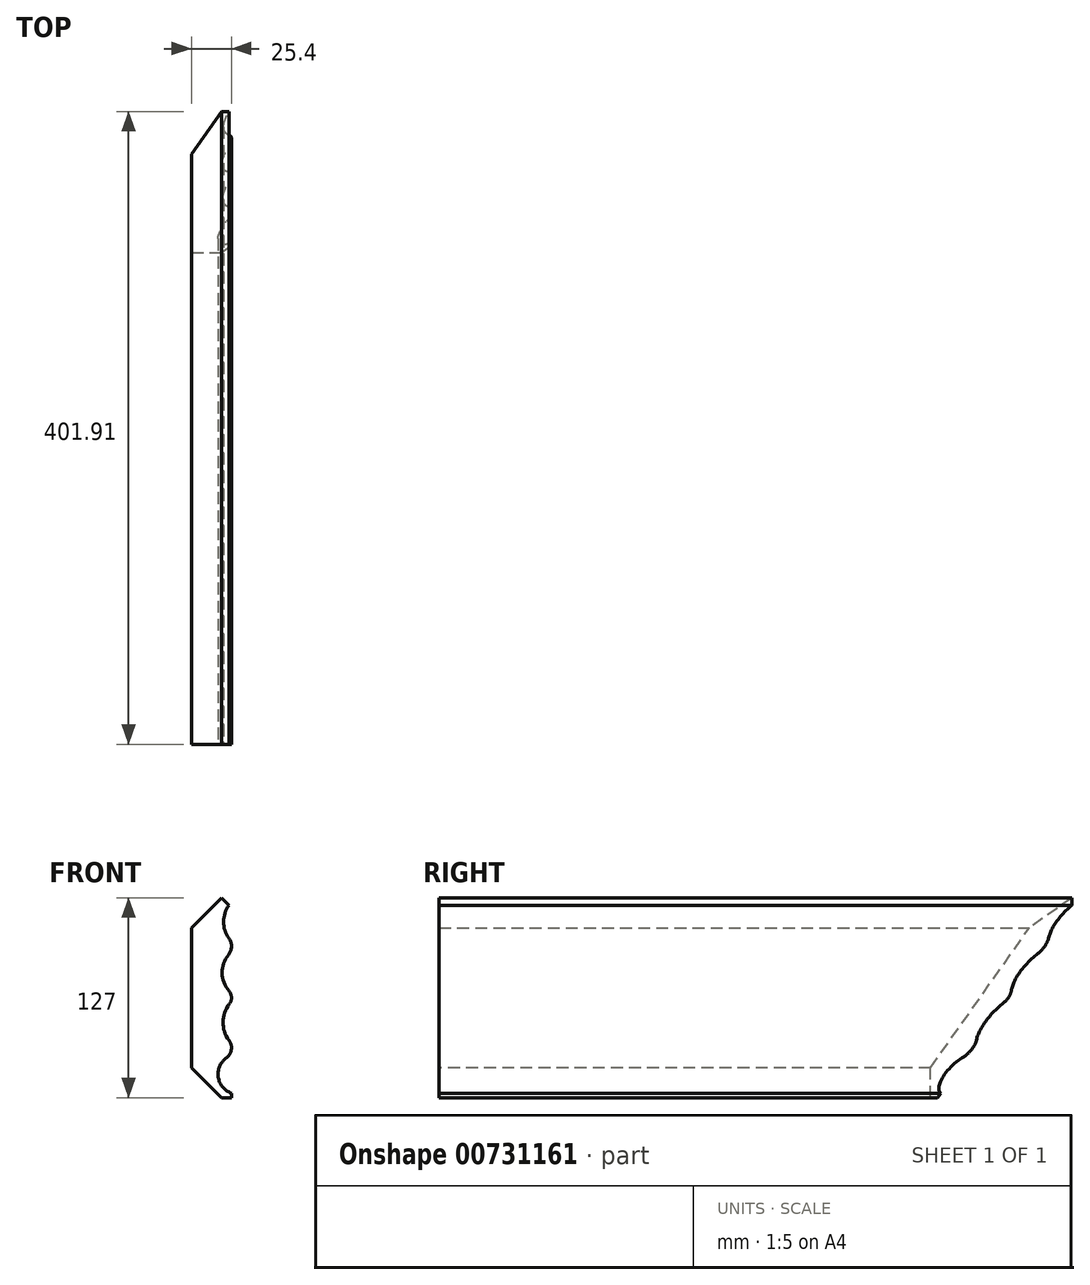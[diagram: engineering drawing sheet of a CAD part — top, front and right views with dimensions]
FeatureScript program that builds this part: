
annotation { "Feature Type Name" : "Feature", "Feature Type Description" : "" }
export const myFeature = defineFeature(function(context is Context, id is Id, definition is map)
    precondition{}
    {
        {
            var Q0;
            Q0=qCreatedBy(makeId("Front.planeOp"),FACE);
            var sketch = newSketch(context, id + "F0", { "sketchPlane" : qUnion([Q0])});
            skLineSegment(sketch, "E0.bottom", {"start": v(12.7, -63.5) * mm, "end": v(-12.7, -63.5) * mm});
            skLineSegment(sketch, "E0.top", {"start": v(12.7, 63.5) * mm, "end": v(-12.7, 63.5) * mm});
            skLineSegment(sketch, "E0.left", {"start": v(12.7, -63.5) * mm, "end": v(12.7, 63.5) * mm});
            skLineSegment(sketch, "E0.right", {"start": v(-12.7, -63.5) * mm, "end": v(-12.7, 63.5) * mm});
            skPoint(sketch, "E0.middle", {"position": v(0, 0) * mm});
            skSolve(sketch);
        }
        {
            var Q0;
            Q0 = qSketchRegion(id + "F0", true);
            extrude(context, id + "F1", {"entities" : qUnion([Q0]), "endBound" : BoundingType.SYMMETRIC, "oppositeDirection" : true, "depth" : 406.4 * mm, "offsetDistance" : 25.4 * mm});
        }
        {
            var Q0;
            Q0=makeQuery(id+"F1.opExtrude","SWEPT_EDGE",EDGE,{"disambiguationData":[OSD([sQuery(id+"F0.wireOp",EDGE,"E0.top"),sQuery(id+"F0.wireOp",EDGE,"E0.right")])]});
            var Q1;
            Q1=makeQuery(id+"F1.opExtrude","SWEPT_EDGE",EDGE,{"disambiguationData":[OSD([sQuery(id+"F0.wireOp",EDGE,"E0.bottom"),sQuery(id+"F0.wireOp",EDGE,"E0.right")])]});
            chamfer(context, id + "F2", {"entities" : qUnion([Q0, Q1]), "width" : 19.05 * mm, "tangentPropagation" : true});
        }
        {
            var Q0;
            Q0=makeQuery(id+"F1.opExtrude","CAP_FACE",FACE,{"disambiguationData":[OSD([sQuery(id+"F0.wireOp",EDGE,"E0.bottom"),sQuery(id+"F0.wireOp",EDGE,"E0.top"),sQuery(id+"F0.wireOp",EDGE,"E0.left"),sQuery(id+"F0.wireOp",EDGE,"E0.right")])],"isStart":true});
            var sketch = newSketch(context, id + "F3", { "sketchPlane" : qUnion([Q0])});
            skArc(sketch, "E1", {"start": v(10.78, 27.27) * mm, "mid": v(12.7, 32.47) * mm, "end": v(11.06, 37.77) * mm});
            skArc(sketch, "E2", {"start": v(9.4, -38.33) * mm, "mid": v(12.61, -33.04) * mm, "end": v(11.1, -27.05) * mm});
            skArc(sketch, "E3", {"start": v(11.31, -4.03) * mm, "mid": v(12.7, 0.16) * mm, "end": v(11.12, 4.27) * mm});
            skArc(sketch, "E4", {"start": v(9.4, -38.33) * mm, "mid": v(4.3, -50.48) * mm, "end": v(12.7, -60.62) * mm});
            skLineSegment(sketch, "E5", {"start": v(12.7, 63.5) * mm, "end": v(12.7, -63.5) * mm});
            skArc(sketch, "E6.trimOffspring", {"start": v(11.31, -4.03) * mm, "mid": v(7.31, -15.5) * mm, "end": v(11.1, -27.05) * mm});
            skArc(sketch, "E7.trimOffspring", {"start": v(10.78, 27.27) * mm, "mid": v(6.78, 15.7) * mm, "end": v(11.12, 4.27) * mm});
            skArc(sketch, "E8.trimOffspring", {"start": v(12.7, 60.57) * mm, "mid": v(7.73, 49.47) * mm, "end": v(11.06, 37.77) * mm});
            skSolve(sketch);
        }
        {
            var Q0;
            {var subQ0=sQuery(id+"F3.wireOp",EDGE,"E8.trimOffspring");Q0=makeQuery(id+"F3.imprint","IMPRINT",FACE,{"disambiguationData":[TD([[makeQuery(id+"F3.imprint","IMPRINT",EDGE,{"derivedFrom":subQ0}),1.0]])]});}
            var Q1;
            {var subQ0=sQuery(id+"F3.wireOp",EDGE,"E7.trimOffspring");Q1=makeQuery(id+"F3.imprint","IMPRINT",FACE,{"disambiguationData":[TD([[makeQuery(id+"F3.imprint","IMPRINT",EDGE,{"derivedFrom":subQ0}),1.0]])]});}
            var Q2;
            {var subQ0=sQuery(id+"F3.wireOp",EDGE,"E6.trimOffspring");Q2=makeQuery(id+"F3.imprint","IMPRINT",FACE,{"disambiguationData":[TD([[makeQuery(id+"F3.imprint","IMPRINT",EDGE,{"derivedFrom":subQ0}),1.0]])]});}
            var Q3;
            {var subQ0=sQuery(id+"F3.wireOp",EDGE,"E4");Q3=makeQuery(id+"F3.imprint","IMPRINT",FACE,{"disambiguationData":[TD([[makeQuery(id+"F3.imprint","IMPRINT",EDGE,{"derivedFrom":subQ0}),1.0]])]});}
            extrude(context, id + "F4", {"entities" : qUnion([Q0, Q1, Q2, Q3]), "operationType" : NewBodyOperationType.REMOVE, "endBound" : BoundingType.THROUGH_ALL, "oppositeDirection" : true, "depth" : 25.4 * mm, "offsetDistance" : 25.4 * mm});
        }
        {
            var Q0;
            Q0=makeQuery(id+"F2.opChamfer","BLEND_FACE",FACE,{"disambiguationData":[OSD([sQuery(id+"F0.wireOp",EDGE,"E0.top"),sQuery(id+"F0.wireOp",EDGE,"E0.right")])]});
            var sketch = newSketch(context, id + "F5", { "sketchPlane" : qUnion([Q0])});
            skLineSegment(sketch, "E9.0.0", {"start": v(-203.2, 53.88) * mm, "end": v(-203.2, 49.4) * mm});
            skLineSegment(sketch, "E9.0.1", {"start": v(-203.2, 49.4) * mm, "end": v(203.2, 49.4) * mm});
            skLineSegment(sketch, "E9.0.2", {"start": v(203.2, 49.4) * mm, "end": v(203.2, 53.88) * mm});
            skLineSegment(sketch, "E9.0.3", {"start": v(203.2, 53.88) * mm, "end": v(-203.2, 53.88) * mm});
            skLineSegment(sketch, "E10", {"start": v(-203.2, 53.88) * mm, "end": v(-70.85, -78.47) * mm});
            skLineSegment(sketch, "E11", {"start": v(-70.85, -78.47) * mm, "end": v(-203.2, -78.47) * mm});
            skLineSegment(sketch, "E12", {"start": v(-203.2, 49.4) * mm, "end": v(-203.2, -78.47) * mm});
            skSolve(sketch);
        }
        {
            var Q0;
            {var subQ0=sQuery(id+"F5.wireOp",EDGE,"E9.0.2");Q0=makeQuery(id+"F5.imprint","IMPRINT",FACE,{"disambiguationData":[TD([[makeQuery(id+"F5.imprint","IMPRINT",EDGE,{"derivedFrom":subQ0}),1.0]])]});}
            var Q1;
            {var subQ0=sQuery(id+"F5.wireOp",EDGE,"E9.0.0");Q1=makeQuery(id+"F5.imprint","IMPRINT",FACE,{"disambiguationData":[TD([[makeQuery(id+"F5.imprint","IMPRINT",EDGE,{"derivedFrom":subQ0}),1.0]])]});}
            var Q2;
            {var subQ1=sQuery(id+"F5.wireOp",EDGE,"E9.0.1");var subQ3=sQuery(id+"F5.wireOp",EDGE,"E10");var subQ4=makeQuery(id+"F5.imprint","INTERSECT",VERTEX,{"derivedFrom":[subQ1,subQ3]});Q2=makeQuery(id+"F5.imprint","IMPRINT",FACE,{"disambiguationData":[TD([[makeQuery(id+"F5.imprint","IMPRINT",EDGE,{"disambiguationData":[TD([[subQ4,1.0]])],"derivedFrom":subQ1}),-1.0]])]});}
            var Q3;
            {var subQ0=sQuery(id+"F5.wireOp",EDGE,"E11");Q3=makeQuery(id+"F5.imprint","IMPRINT",FACE,{"disambiguationData":[TD([[makeQuery(id+"F5.imprint","IMPRINT",EDGE,{"derivedFrom":subQ0}),-1.0]])]});}
            extrude(context, id + "F6", {"entities" : qUnion([Q0, Q1, Q2, Q3]), "operationType" : NewBodyOperationType.REMOVE, "endBound" : BoundingType.THROUGH_ALL, "oppositeDirection" : true, "depth" : 25.4 * mm, "offsetDistance" : 25.4 * mm});
        }
    });
